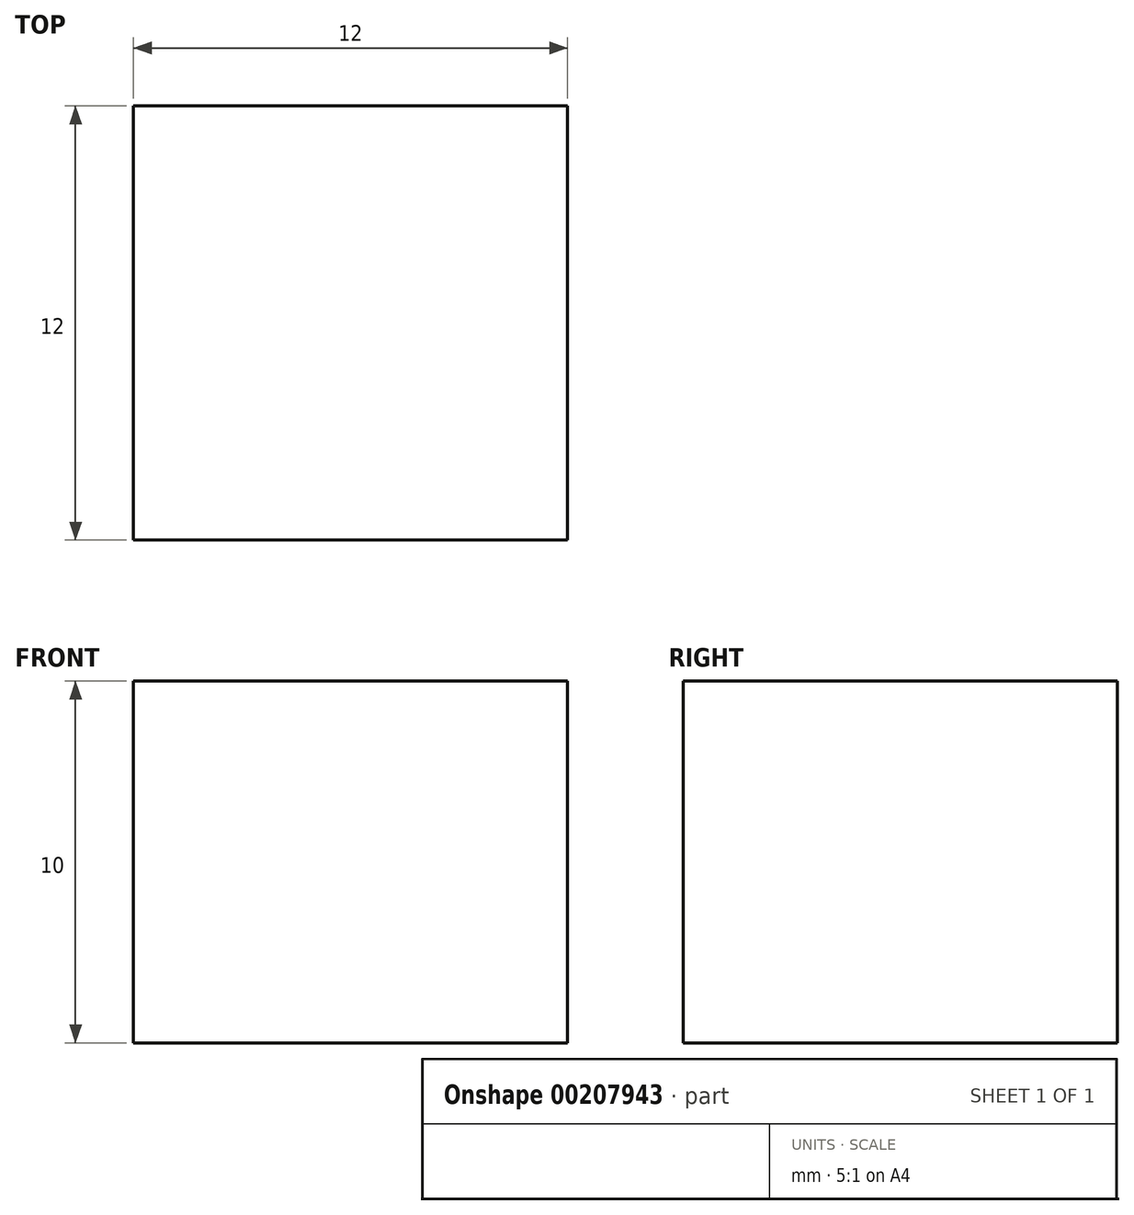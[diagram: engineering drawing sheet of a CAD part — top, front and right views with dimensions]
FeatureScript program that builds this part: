
annotation { "Feature Type Name" : "Feature", "Feature Type Description" : "" }
export const myFeature = defineFeature(function(context is Context, id is Id, definition is map)
    precondition{}
    {
        {
            var Q0;
            Q0=qCreatedBy(makeId("Top.planeOp"),FACE);
            var sketch = newSketch(context, id + "F0", { "sketchPlane" : qUnion([Q0])});
            skLineSegment(sketch, "E0.bottom", {"start": v(5, 5) * mm, "end": v(-5, 5) * mm});
            skLineSegment(sketch, "E0.top", {"start": v(5, -5) * mm, "end": v(-5, -5) * mm});
            skLineSegment(sketch, "E0.left", {"start": v(5, 5) * mm, "end": v(5, -5) * mm});
            skLineSegment(sketch, "E0.right", {"start": v(-5, 5) * mm, "end": v(-5, -5) * mm});
            skPoint(sketch, "E0.middle", {"position": v(0, 0) * mm});
            skLineSegment(sketch, "E1.0", {"start": v(6, 6) * mm, "end": v(-6, 6) * mm});
            skLineSegment(sketch, "E1.1", {"start": v(6, 6) * mm, "end": v(6, -6) * mm});
            skLineSegment(sketch, "E1.2", {"start": v(6, -6) * mm, "end": v(-6, -6) * mm});
            skLineSegment(sketch, "E1.3", {"start": v(-6, 6) * mm, "end": v(-6, -6) * mm});
            skSolve(sketch);
        }
        {
            var Q0;
            Q0=makeQuery(id+"F0.imprint","IMPRINT",FACE,{"disambiguationData":[TD([[makeQuery(id+"F0.imprint","IMPRINT",EDGE,{"derivedFrom":sQuery(id+"F0.wireOp",EDGE,"E0.bottom")}),-1.0]])]});
            var Q1;
            Q1=makeQuery(id+"F0.imprint","IMPRINT",FACE,{"disambiguationData":[TD([[makeQuery(id+"F0.imprint","IMPRINT",EDGE,{"derivedFrom":sQuery(id+"F0.wireOp",EDGE,"E0.bottom")}),1.0]])]});
            extrude(context, id + "F1", {"entities" : qUnion([Q0, Q1]), "depth" : 10 * mm});
        }
    });
